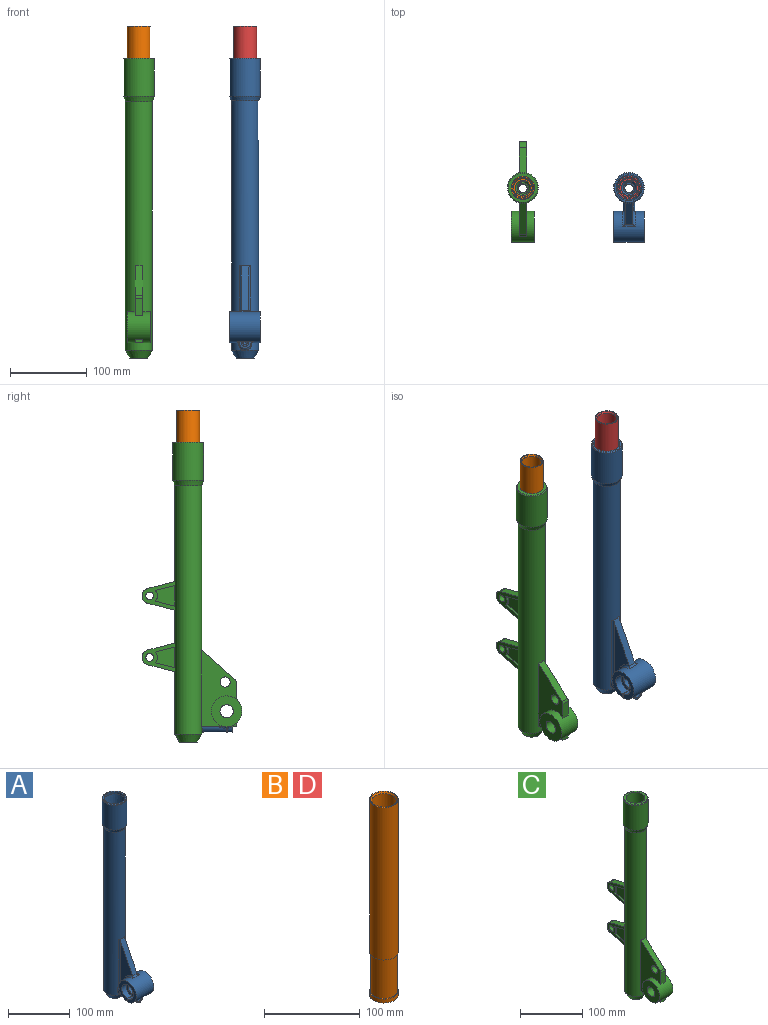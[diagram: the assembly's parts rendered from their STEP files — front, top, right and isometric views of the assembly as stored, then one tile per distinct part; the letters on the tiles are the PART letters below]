
ASSEMBLY  parts=4 mates=4
PART A: 62 faces, bbox 40.3x90.5x390.3 mm
  f0: cylinder r=17.5mm len=352.25mm, axis (0,0,-1), area 37146.7mm2, adj f2,f20,f30,f33,f43,f44,f48,f49
  f1: cone r=7.5mm half-angle=45deg, axis (0,0,1), area 725.9mm2, adj f15,f16,f60
  f2: cone r=17.5mm half-angle=30deg, axis (0,0,1), area 987.3mm2, adj f0,f14,f46,f59
  f3: cylinder r=20mm len=40mm, axis (-1,0,0), area 3812.4mm2, adj f4,f5,f12,f37,f38,f39,f42,f45
  f4: plane 40x39.99mm, normal (1,0,0), area 1011.8mm2, adj f3,f6,f38,f39
  f5: plane 40x39.99mm, normal (-1,0,0), area 677.6mm2, adj f3,f8,f38,f39
  f6: cylinder r=8.62mm len=30mm, axis (-1,0,0), area 1594.8mm2, adj f4,f7,f38,f39
  f7: plane 27x26.99mm, normal (-1,0,0), area 334.2mm2, adj f6,f8,f38,f39
  f8: cylinder r=13.5mm len=27mm, axis (-1,0,0), area 838.2mm2, adj f5,f7,f38,f39
  f9: cylinder r=7.5mm len=14.79mm, axis (0,-1,0), area 141mm2, adj f12,f39,f42,f56
  f10: cylinder r=2.75mm len=5.5mm, axis (0,-1,0), area 34.6mm2, adj f35,f39
  f11: plane 58.43x29.26mm, normal (0,-0.89,0.45), area 653.2mm2, adj f30,f31,f32,f33,f43,f47,f48,f50
  f12: plane 21.14x9.26mm, normal (0,-1,0), area 62.5mm2, adj f3,f9,f36,f42,f56
  f13: cone r=15mm half-angle=5.6deg, axis (0,0,1), area 2145.8mm2, adj f15,f23
  f14: plane 23.45x23.45mm, normal (0,0,-1), area 141mm2, adj f2,f58
  f15: cylinder r=15mm len=347mm, axis (0,0,1), area 31684.5mm2, adj f1,f13,f26,f27,f28,f29
  f16: plane 15x15mm, normal (0,0,1), area 81.7mm2, adj f1,f17
  f17: cylinder r=5.5mm len=11mm, axis (0,0,-1), area 172.8mm2, adj f16,f18
  f18: plane 17.25x17.25mm, normal (0,0,-1), area 138.7mm2, adj f17,f19
  f19: cylinder r=8.62mm len=17.25mm, axis (0,0,-1), area 216.8mm2, adj f18,f58
  f20: cone r=17mm half-angle=1deg, axis (0,0,-1), area 3095.1mm2, adj f0,f22
  f21: plane 38x38mm, normal (0,0,1), area 226.2mm2, adj f23,f57
  f22: cone r=18mm half-angle=20deg, axis (0,0,1), area 698.1mm2, adj f20,f24
  f23: cone r=17mm half-angle=1deg, axis (0,0,-1), area 461.3mm2, adj f13,f21
  f24: cylinder r=20mm len=49mm, axis (0,0,1), area 6157.5mm2, adj f22,f57
  f25: plane 100x10mm, normal (0,1,0), area 1000mm2, adj f26,f27,f28,f29
  f26: plane 100x1.68mm, normal (-1,0,0), area 168.3mm2, adj f15,f25,f28,f29
  f27: plane 100x1.68mm, normal (1,0,0), area 168.3mm2, adj f15,f25,f28,f29
  f28: plane 10x2.54mm, normal (0,0,-1), area 22.6mm2, adj f15,f25,f26,f27
  f29: plane 10x2.54mm, normal (0,0,1), area 22.6mm2, adj f15,f25,f26,f27
  f30: plane 6.83x1.39mm, normal (0,0,1), area 1.8mm2, adj f0,f11,f43
  f31: plane 90.45x27.29mm, normal (1,0,0), area 1160.6mm2, adj f11,f48,f52,f53
  f32: plane 91.8x27.43mm, normal (-1,0,0), area 1175.8mm2, adj f11,f34,f43,f44,f45,f47
  f33: plane 6.83x1.39mm, normal (0,0,1), area 1.8mm2, adj f0,f11,f48
  f34: cylinder r=7.5mm len=30.63mm, axis (0,-1,0), area 862.3mm2, adj f32,f38,f44,f45,f46,f49,f53,f55
  f35: plane 9.75x9.75mm, normal (0,-1,0), area 50.9mm2, adj f10,f36
  f36: cylinder r=4.88mm len=9.75mm, axis (0,-1,0), area 153.2mm2, adj f12,f35,f37
  f37: plane 9.3x3.42mm, normal (0,1,0), area 23.3mm2, adj f3,f36
  f38: plane 40.06x18.95mm, normal (0,-1,0), area 473.7mm2, adj f3,f4,f5,f6,f7,f8,f34,f41
  f39: plane 40.06x18.95mm, normal (0,1,0), area 473.7mm2, adj f3,f4,f5,f6,f7,f8,f9,f10
  f40: cone r=0mm half-angle=59deg, axis (0,-1,0), area 27.7mm2, adj f41
  f41: cylinder r=2.75mm len=27mm, axis (0,-1,0), area 466.5mm2, adj f38,f40
  f42: bspline ~11.58x4.47mm, area 28.3mm2, adj f3,f9,f12,f39
  f43: cylinder r=3mm len=94.38mm, axis (0,0,-1), area 327.2mm2, adj f0,f11,f30,f32,f44
  f44: bspline ~19.15x7.69mm, area 63.9mm2, adj f0,f32,f34,f43,f46
  f45: bspline ~21.53x12.48mm, area 92.7mm2, adj f3,f32,f34,f38,f47
  f46: bspline ~7.07x3.52mm, area 20.4mm2, adj f2,f34,f44,f49
  f47: torus R=23mm, axis (1,0,0), area 209.1mm2, adj f3,f11,f32,f45,f50
  f48: cylinder r=3mm len=93.2mm, axis (0,0,-1), area 325.1mm2, adj f0,f11,f31,f33,f51
  f49: bspline ~17.74x7.88mm, area 61.6mm2, adj f0,f34,f46,f51
  f50: cylinder r=3mm len=16mm, axis (-1,0,0), area 45mm2, adj f3,f11,f47,f52
  f51: sphere r=3mm, area 3.6mm2, adj f48,f49,f53
  f52: torus R=23mm, axis (1,0,0), area 206.1mm2, adj f3,f11,f31,f50,f54
  f53: cylinder r=3mm len=12.29mm, axis (0,-1,0), area 26mm2, adj f31,f34,f51,f54
  f54: sphere r=3mm, area 4.8mm2, adj f52,f53,f55
  f55: bspline ~19.92x11.44mm, area 89.2mm2, adj f3,f34,f38,f54
  f56: bspline ~12.06x4.39mm, area 28.3mm2, adj f3,f9,f12,f39
  f57: cone r=19mm half-angle=45deg, axis (0,0,-1), area 173.3mm2, adj f21,f24
  f58: cone r=8.62mm half-angle=45deg, axis (0,0,-1), area 81.1mm2, adj f14,f19
  f59: cylinder r=5mm len=13.32mm, axis (0,0.71,-0.71), area 219.3mm2, adj f0,f2,f61
  f60: cylinder r=2.75mm len=5.5mm, axis (0,0.71,-0.71), area 9.5mm2, adj f1,f61
  f61: plane 10x7.07mm, normal (0,0.71,-0.71), area 54.8mm2, adj f59,f60
PART B: 13 faces, bbox 30x30x250 mm
  f0: cylinder r=10mm len=20mm, axis (0,0,-1), area 188.5mm2, adj f1,f12
  f1: plane 24x24mm, normal (0,0,1), area 138.2mm2, adj f0,f2
  f2: cylinder r=12mm len=218.54mm, axis (0,0,-1), area 16477.2mm2, adj f1,f3
  f3: cone r=12.85mm half-angle=30deg, axis (0,0,1), area 132mm2, adj f2,f4
  f4: cylinder r=12.85mm len=25.69mm, axis (0,0,-1), area 2017.7mm2, adj f3,f5
  f5: cone r=14mm half-angle=30deg, axis (0,0,1), area 194.8mm2, adj f4,f6
  f6: plane 30x30mm, normal (0,0,1), area 91.1mm2, adj f5,f7
  f7: cylinder r=15mm len=195mm, axis (0,0,-1), area 18378.3mm2, adj f6,f8
  f8: plane 30x30mm, normal (0,0,-1), area 91.1mm2, adj f7,f9
  f9: cylinder r=14mm len=50mm, axis (0,0,-1), area 4398.2mm2, adj f8,f10
  f10: plane 30x30mm, normal (0,0,1), area 91.1mm2, adj f9,f11
  f11: cylinder r=15mm len=30mm, axis (0,0,-1), area 471.2mm2, adj f10,f12
  f12: plane 30x30mm, normal (0,0,-1), area 392.7mm2, adj f0,f11
PART C: 82 faces, bbox 40x130x390 mm
  f0: cone r=7.5mm half-angle=45deg, axis (0,0,1), area 727.9mm2, adj f10,f11,f79
  f1: cylinder r=8.62mm len=17.25mm, axis (0,0,-1), area 215.8mm2, adj f13,f32,f81
  f2: cone r=17.5mm half-angle=30deg, axis (0,0,1), area 978.2mm2, adj f7,f9,f81
  f3: plane 12.5x4.39mm, normal (1,0,0), area 17.4mm2, adj f5,f26,f27
  f4: plane 12.5x4.39mm, normal (-1,0,0), area 17.4mm2, adj f5,f26,f27
  f5: plane 10x4.39mm, normal (0,-1,0), area 43.9mm2, adj f3,f4,f26,f27
  f6: plane 22.14x10mm, normal (0,-1,0), area 221.4mm2, adj f22,f23,f27,f78
  f7: cylinder r=17.5mm len=323.13mm, axis (0,0,-1), area 34039.1mm2, adj f2,f14,f21,f22,f23,f24,f26,f33
  f8: plane 38x38mm, normal (0,0,1), area 427.3mm2, adj f10,f31
  f9: plane 23.45x23.45mm, normal (0,0,-1), area 141mm2, adj f2,f32
  f10: cylinder r=15mm len=372.5mm, axis (0,0,1), area 34087.8mm2, adj f0,f8,f17,f18,f19,f20
  f11: plane 15x14.78mm, normal (0,0,1), area 78.8mm2, adj f0,f12,f79
  f12: cylinder r=5.5mm len=11mm, axis (0,0,-1), area 172.8mm2, adj f11,f13
  f13: plane 17.25x17.11mm, normal (0,0,-1), area 137.7mm2, adj f1,f12,f81
  f14: cone r=17mm half-angle=20deg, axis (0,0,1), area 861.1mm2, adj f7,f15
  f15: cylinder r=20mm len=49mm, axis (0,0,1), area 6157.5mm2, adj f14,f31
  f16: plane 100x10mm, normal (0,1,0), area 1000mm2, adj f17,f18,f19,f20
  f17: plane 100x1.64mm, normal (-1,0,0), area 163.6mm2, adj f10,f16,f19,f20
  f18: plane 100x1.64mm, normal (1,0,0), area 163.6mm2, adj f10,f16,f19,f20
  f19: plane 10x2.49mm, normal (0,0,-1), area 22.1mm2, adj f10,f16,f17,f18
  f20: plane 10x2.49mm, normal (0,0,1), area 22.1mm2, adj f10,f16,f17,f18
  f21: plane 5x0.73mm, normal (0,0,1), area 1.2mm2, adj f7,f23,f25
  f22: plane 100x45.73mm, normal (1,0,0), area 2424.5mm2, adj f6,f7,f24,f25,f26,f27,f77,f78
  f23: plane 100x45.73mm, normal (-1,0,0), area 2424.5mm2, adj f6,f7,f21,f25,f26,f27,f77,f78
  f24: plane 5x0.73mm, normal (0,0,1), area 1.2mm2, adj f7,f22,f25
  f25: plane 43.32x38.51mm, normal (0,-0.66,0.75), area 579.6mm2, adj f21,f22,f23,f24,f78
  f26: plane 45.73x10mm, normal (0,0,-1), area 452.4mm2, adj f3,f4,f5,f7,f22,f23
  f27: cylinder r=20mm len=40mm, axis (-1,0,0), area 2871.5mm2, adj f3,f4,f5,f6,f22,f23,f28,f29
  f28: plane 40x40mm, normal (1,0,0), area 1023.2mm2, adj f27,f30
  f29: plane 40x40mm, normal (-1,0,0), area 1023.2mm2, adj f27,f30
  f30: cylinder r=8.62mm len=30mm, axis (-1,0,0), area 1624.8mm2, adj f28,f29
  f31: cone r=19mm half-angle=45deg, axis (0,0,-1), area 173.3mm2, adj f8,f15
  f32: cone r=8.62mm half-angle=45deg, axis (0,0,-1), area 81.1mm2, adj f1,f9
  f33: plane 43.23x37mm, normal (-1,0,0), area 535.8mm2, adj f7,f42,f43,f44,f45,f46,f47,f48
  f34: plane 43.23x37mm, normal (1,0,0), area 535.8mm2, adj f7,f37,f38,f39,f40,f41,f45,f46
  f35: plane 26.69x25.5mm, normal (1,0,0), area 492mm2, adj f7,f39,f40,f41,f51,f53
  f36: plane 26.69x25.5mm, normal (-1,0,0), area 492mm2, adj f7,f42,f43,f44,f49,f52
  f37: plane 5x0.73mm, normal (0,0,1), area 1.2mm2, adj f7,f34,f47
  f38: plane 5x0.73mm, normal (0,0,-1), area 1.2mm2, adj f7,f34,f45
  f39: plane 25.32x6.38mm, normal (0,-0.24,-0.97), area 65.3mm2, adj f34,f35,f41,f51
  f40: plane 25.32x6.38mm, normal (0,-0.24,0.97), area 65.3mm2, adj f34,f35,f41,f53
  f41: cylinder r=10mm len=13.93mm, axis (1,0,0), area 38.5mm2, adj f34,f35,f39,f40
  f42: plane 25.32x6.38mm, normal (0,-0.24,-0.97), area 65.3mm2, adj f33,f36,f43,f49
  f43: cylinder r=10mm len=13.93mm, axis (1,0,0), area 38.5mm2, adj f33,f36,f42,f44
  f44: plane 25.32x6.38mm, normal (0,-0.24,0.97), area 65.3mm2, adj f33,f36,f43,f52
  f45: plane 34.94x10mm, normal (0,0.24,-0.97), area 360.3mm2, adj f33,f34,f38,f46,f54
  f46: cylinder r=10mm len=19.39mm, axis (1,0,0), area 264.8mm2, adj f33,f34,f45,f47
  f47: plane 34.94x10mm, normal (0,0.24,0.97), area 360.3mm2, adj f33,f34,f37,f46,f50
  f48: cylinder r=5mm len=10mm, axis (1,0,0), area 314.2mm2, adj f33,f34
  f49: plane 2.5x0.73mm, normal (0,0,-1), area 1.1mm2, adj f7,f33,f36,f42
  f50: plane 5x0.73mm, normal (0,0,1), area 1.2mm2, adj f7,f33,f47
  f51: plane 2.5x0.73mm, normal (0,0,-1), area 1.1mm2, adj f7,f34,f35,f39
  f52: plane 2.5x0.73mm, normal (0,0,1), area 1.1mm2, adj f7,f33,f36,f44
  f53: plane 2.5x0.73mm, normal (0,0,1), area 1.1mm2, adj f7,f34,f35,f40
  f54: plane 5x0.73mm, normal (0,0,-1), area 1.2mm2, adj f7,f33,f45
  f55: plane 43.23x37mm, normal (-1,0,0), area 535.8mm2, adj f7,f64,f65,f66,f67,f68,f69,f70
  f56: plane 43.23x37mm, normal (1,0,0), area 535.8mm2, adj f7,f59,f60,f61,f62,f63,f67,f68
  f57: plane 26.69x25.5mm, normal (1,0,0), area 492mm2, adj f7,f61,f62,f63,f73,f75
  f58: plane 26.69x25.5mm, normal (-1,0,0), area 492mm2, adj f7,f64,f65,f66,f71,f74
  f59: plane 5x0.73mm, normal (0,0,1), area 1.2mm2, adj f7,f56,f69
  f60: plane 5x0.73mm, normal (0,0,-1), area 1.2mm2, adj f7,f56,f67
  f61: plane 25.32x6.38mm, normal (0,-0.24,-0.97), area 65.3mm2, adj f56,f57,f63,f73
  f62: plane 25.32x6.38mm, normal (0,-0.24,0.97), area 65.3mm2, adj f56,f57,f63,f75
  f63: cylinder r=10mm len=13.93mm, axis (1,0,0), area 38.5mm2, adj f56,f57,f61,f62
  f64: plane 25.32x6.38mm, normal (0,-0.24,-0.97), area 65.3mm2, adj f55,f58,f65,f71
  f65: cylinder r=10mm len=13.93mm, axis (1,0,0), area 38.5mm2, adj f55,f58,f64,f66
  f66: plane 25.32x6.38mm, normal (0,-0.24,0.97), area 65.3mm2, adj f55,f58,f65,f74
  f67: plane 34.94x10mm, normal (0,0.24,-0.97), area 360.3mm2, adj f55,f56,f60,f68,f76
  f68: cylinder r=10mm len=19.39mm, axis (1,0,0), area 264.8mm2, adj f55,f56,f67,f69
  f69: plane 34.94x10mm, normal (0,0.24,0.97), area 360.3mm2, adj f55,f56,f59,f68,f72
  f70: cylinder r=5mm len=10mm, axis (1,0,0), area 314.2mm2, adj f55,f56
  f71: plane 2.5x0.73mm, normal (0,0,-1), area 1.1mm2, adj f7,f55,f58,f64
  f72: plane 5x0.73mm, normal (0,0,1), area 1.2mm2, adj f7,f55,f69
  f73: plane 2.5x0.73mm, normal (0,0,-1), area 1.1mm2, adj f7,f56,f57,f61
  f74: plane 2.5x0.73mm, normal (0,0,1), area 1.1mm2, adj f7,f55,f58,f66
  f75: plane 2.5x0.73mm, normal (0,0,1), area 1.1mm2, adj f7,f56,f57,f62
  f76: plane 5x0.73mm, normal (0,0,-1), area 1.2mm2, adj f7,f55,f67
  f77: cylinder r=6.6mm len=13.2mm, axis (1,0,0), area 414.7mm2, adj f22,f23
  f78: cylinder r=5mm len=10mm, axis (1,0,0), area 42.2mm2, adj f6,f22,f23,f25
  f79: cylinder r=2.75mm len=5.97mm, axis (0,0.71,-0.71), area 41.3mm2, adj f0,f11,f80
  f80: plane 10x7.07mm, normal (0,0.71,-0.71), area 54.8mm2, adj f79,f81
  f81: cylinder r=5mm len=12.5mm, axis (0,0.71,-0.71), area 185.7mm2, adj f1,f2,f13,f80
PART D: same geometry as B
PLACE A at identity fixed
PLACE B t=(-138,0,181.63)mm
PLACE C t=(-138,0,0)mm
PLACE D t=(0,0,181.63)mm
MATE slider B.f0 <-> C.f0  axis (0,0,-1) through (-138,0,334.13)mm
MATE fastened A.f3 <-> C.f27  axis (1,0,0) through (20,-50,40)mm
MATE slider D.f0 <-> A.f0  axis (0,0,-1) through (0,0,334.13)mm
MATE planar D.f0 <-> B.f0  axis (0,0,1) through (0,0,431.63)mm
